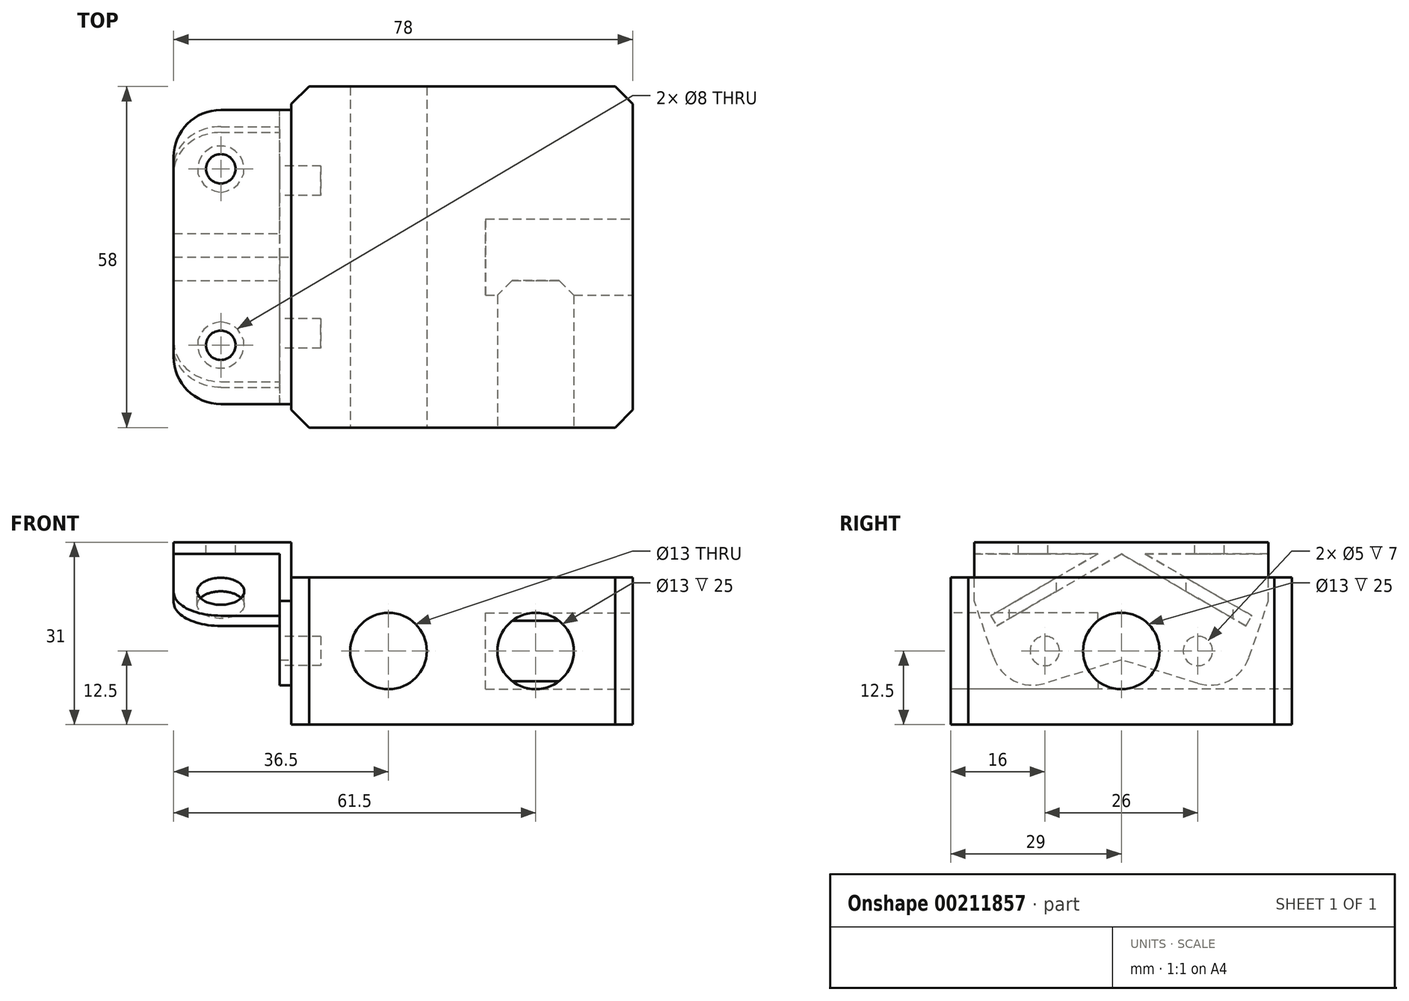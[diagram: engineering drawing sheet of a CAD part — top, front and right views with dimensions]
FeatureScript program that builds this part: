
annotation { "Feature Type Name" : "Feature", "Feature Type Description" : "" }
export const myFeature = defineFeature(function(context is Context, id is Id, definition is map)
    precondition{}
    {
        {
            var Q0;
            Q0=qCreatedBy(makeId("Top.planeOp"),FACE);
            var sketch = newSketch(context, id + "F0", { "sketchPlane" : qUnion([Q0])});
            skLineSegment(sketch, "E0.bottom", {"start": v(-29, 29) * mm, "end": v(29, 29) * mm});
            skLineSegment(sketch, "E0.top", {"start": v(-29, -29) * mm, "end": v(29, -29) * mm});
            skLineSegment(sketch, "E0.left", {"start": v(-29, 29) * mm, "end": v(-29, -29) * mm});
            skLineSegment(sketch, "E0.right", {"start": v(29, 29) * mm, "end": v(29, -29) * mm});
            skLineSegment(sketch, "E1", {"start": v(0, 0) * mm, "end": v(29, 0) * mm, "construction": true});
            skLineSegment(sketch, "E2", {"start": v(0, 0) * mm, "end": v(0, -29) * mm, "construction": true});
            skLineSegment(sketch, "E3", {"start": v(0, 0) * mm, "end": v(0, 29) * mm, "construction": true});
            skLineSegment(sketch, "E4", {"start": v(0, 0) * mm, "end": v(-29, 0) * mm, "construction": true});
            skSolve(sketch);
        }
        {
            var Q0;
            Q0 = qSketchRegion(id + "F0", true);
            extrude(context, id + "F1", {"entities" : qUnion([Q0]), "depth" : 25 * mm});
        }
        {
            var Q0;
            Q0=makeQuery(id+"F1.opExtrude","SWEPT_EDGE",EDGE,{"disambiguationData":[OSD([sQuery(id+"F0.wireOp",EDGE,"E0.top"),sQuery(id+"F0.wireOp",EDGE,"E0.left")])]});
            var Q1;
            Q1=makeQuery(id+"F1.opExtrude","SWEPT_EDGE",EDGE,{"disambiguationData":[OSD([sQuery(id+"F0.wireOp",EDGE,"E0.top"),sQuery(id+"F0.wireOp",EDGE,"E0.right")])]});
            var Q2;
            Q2=makeQuery(id+"F1.opExtrude","SWEPT_EDGE",EDGE,{"disambiguationData":[OSD([sQuery(id+"F0.wireOp",EDGE,"E0.bottom"),sQuery(id+"F0.wireOp",EDGE,"E0.right")])]});
            var Q3;
            Q3=makeQuery(id+"F1.opExtrude","SWEPT_EDGE",EDGE,{"disambiguationData":[OSD([sQuery(id+"F0.wireOp",EDGE,"E0.bottom"),sQuery(id+"F0.wireOp",EDGE,"E0.left")])]});
            chamfer(context, id + "F2", {"entities" : qUnion([Q0, Q1, Q2, Q3]), "width" : 3 * mm, "tangentPropagation" : true});
        }
        {
            var Q0;
            Q0=makeQuery(id+"F1.opExtrude","SWEPT_FACE",FACE,{"disambiguationData":[OSD([sQuery(id+"F0.wireOp",EDGE,"E0.top")])]});
            var sketch = newSketch(context, id + "F3", { "sketchPlane" : qUnion([Q0])});
            skCircle(sketch, "E5", {"center": v(-12.5, 12.5) * mm, "radius": 6.5 * mm});
            skCircle(sketch, "E6", {"center": v(12.5, 12.5) * mm, "radius": 6.5 * mm});
            skLineSegment(sketch, "E7", {"start": v(12.5, 12.5) * mm, "end": v(0, 12.5) * mm, "construction": true});
            skLineSegment(sketch, "E8", {"start": v(0, 12.5) * mm, "end": v(-12.5, 12.5) * mm, "construction": true});
            skLineSegment(sketch, "E9", {"start": v(0, 12.5) * mm, "end": v(0, 0) * mm, "construction": true});
            skLineSegment(sketch, "E10", {"start": v(0, 12.5) * mm, "end": v(0, 25) * mm, "construction": true});
            skSolve(sketch);
        }
        {
            var Q0;
            Q0=makeQuery(id+"F3.imprint","IMPRINT",FACE,{"disambiguationData":[TD([[makeQuery(id+"F3.imprint","IMPRINT",EDGE,{"derivedFrom":sQuery(id+"F3.wireOp",EDGE,"E5")}),1.0]])]});
            extrude(context, id + "F4", {"entities" : qUnion([Q0]), "operationType" : NewBodyOperationType.REMOVE, "endBound" : BoundingType.THROUGH_ALL, "oppositeDirection" : true, "depth" : 25 * mm});
        }
        {
            var Q0;
            Q0=makeQuery(id+"F3.imprint","IMPRINT",FACE,{"disambiguationData":[TD([[makeQuery(id+"F3.imprint","IMPRINT",EDGE,{"derivedFrom":sQuery(id+"F3.wireOp",EDGE,"E6")}),1.0]])]});
            extrude(context, id + "F5", {"entities" : qUnion([Q0]), "operationType" : NewBodyOperationType.REMOVE, "oppositeDirection" : true, "depth" : 25 * mm});
        }
        {
            var Q0;
            Q0=makeQuery(id+"F1.opExtrude","SWEPT_FACE",FACE,{"disambiguationData":[OSD([sQuery(id+"F0.wireOp",EDGE,"E0.right")])]});
            var sketch = newSketch(context, id + "F6", { "sketchPlane" : qUnion([Q0])});
            skCircle(sketch, "E11", {"center": v(0, 12.5) * mm, "radius": 6.5 * mm});
            skLineSegment(sketch, "E12", {"start": v(0, 25) * mm, "end": v(0, 12.5) * mm, "construction": true});
            skLineSegment(sketch, "E13", {"start": v(0, 12.5) * mm, "end": v(0, 0) * mm, "construction": true});
            skSolve(sketch);
        }
        {
            var Q0;
            Q0=makeQuery(id+"F6.imprint","IMPRINT",FACE,{"disambiguationData":[TD([[makeQuery(id+"F6.imprint","IMPRINT",EDGE,{"derivedFrom":sQuery(id+"F6.wireOp",EDGE,"E11")}),1.0]])]});
            extrude(context, id + "F7", {"entities" : qUnion([Q0]), "operationType" : NewBodyOperationType.REMOVE, "oppositeDirection" : true, "depth" : 25 * mm});
        }
        {
            var Q0;
            Q0=makeQuery(id+"F1.opExtrude","SWEPT_FACE",FACE,{"disambiguationData":[OSD([sQuery(id+"F0.wireOp",EDGE,"E0.left")])]});
            var sketch = newSketch(context, id + "F8", { "sketchPlane" : qUnion([Q0])});
            skCircle(sketch, "E14", {"center": v(-13, 12.5) * mm, "radius": 2.5 * mm});
            skCircle(sketch, "E15", {"center": v(13, 12.5) * mm, "radius": 2.5 * mm});
            skLineSegment(sketch, "E16", {"start": v(13, 12.5) * mm, "end": v(0, 12.5) * mm, "construction": true});
            skLineSegment(sketch, "E17", {"start": v(0, 12.5) * mm, "end": v(-13, 12.5) * mm, "construction": true});
            skLineSegment(sketch, "E18", {"start": v(0, 12.5) * mm, "end": v(0, 25) * mm, "construction": true});
            skLineSegment(sketch, "E19", {"start": v(0, 12.5) * mm, "end": v(0, 0) * mm, "construction": true});
            skSolve(sketch);
        }
        {
            var Q0;
            Q0=makeQuery(id+"F8.imprint","IMPRINT",FACE,{"disambiguationData":[TD([[makeQuery(id+"F8.imprint","IMPRINT",EDGE,{"derivedFrom":sQuery(id+"F8.wireOp",EDGE,"E14")}),1.0]])]});
            var Q1;
            Q1=makeQuery(id+"F8.imprint","IMPRINT",FACE,{"disambiguationData":[TD([[makeQuery(id+"F8.imprint","IMPRINT",EDGE,{"derivedFrom":sQuery(id+"F8.wireOp",EDGE,"E15")}),1.0]])]});
            extrude(context, id + "F9", {"entities" : qUnion([Q0, Q1]), "operationType" : NewBodyOperationType.REMOVE, "oppositeDirection" : true, "depth" : 5 * mm});
        }
        {
            var Q0;
            Q0=makeQuery(id+"F1.opExtrude","SWEPT_FACE",FACE,{"disambiguationData":[OSD([sQuery(id+"F0.wireOp",EDGE,"E0.left")])]});
            var sketch = newSketch(context, id + "F10", { "sketchPlane" : qUnion([Q0])});
            skLineSegment(sketch, "E20", {"start": v(-21.7, 11.41) * mm, "end": v(-25, 21) * mm});
            skLineSegment(sketch, "E21", {"start": v(-13.03, 7) * mm, "end": v(0, 11) * mm});
            skLineSegment(sketch, "E22", {"start": v(0, 11) * mm, "end": v(13.03, 7) * mm});
            skLineSegment(sketch, "E23", {"start": v(21.7, 11.41) * mm, "end": v(25, 21) * mm});
            skLineSegment(sketch, "E24", {"start": v(25, 21) * mm, "end": v(25, 31) * mm});
            skLineSegment(sketch, "E25", {"start": v(-25, 21) * mm, "end": v(-25, 31) * mm});
            skLineSegment(sketch, "E26", {"start": v(-25, 31) * mm, "end": v(0, 31) * mm});
            skLineSegment(sketch, "E27", {"start": v(0, 31) * mm, "end": v(25, 31) * mm});
            skPoint(sketch, "E28.visualSharp", {"position": v(-19.5, 5.01) * mm});
            skArc(sketch, "E28.filletArc", {"start": v(-21.7, 11.41) * mm, "mid": v(-18.25, 7.45) * mm, "end": v(-13.03, 7) * mm});
            skPoint(sketch, "E29.visualSharp", {"position": v(19.5, 5.01) * mm});
            skArc(sketch, "E29.filletArc", {"start": v(13.03, 7) * mm, "mid": v(18.25, 7.45) * mm, "end": v(21.7, 11.41) * mm});
            skLineSegment(sketch, "E30", {"start": v(15.08, 13.7) * mm, "end": v(0, 13.7) * mm, "construction": true});
            skLineSegment(sketch, "E31", {"start": v(0, 13.7) * mm, "end": v(-15.08, 13.7) * mm, "construction": true});
            skCircle(sketch, "E32", {"center": v(-13, 12.5) * mm, "radius": 3.5 * mm, "construction": true});
            skCircle(sketch, "E33", {"center": v(13, 12.5) * mm, "radius": 3.5 * mm, "construction": true});
            skLineSegment(sketch, "E34", {"start": v(-25, 29) * mm, "end": v(25, 29) * mm});
            skLineSegment(sketch, "E35", {"start": v(-22.19, 18.5) * mm, "end": v(-21.19, 16.77) * mm});
            skLineSegment(sketch, "E36", {"start": v(-21.19, 16.77) * mm, "end": v(0, 29) * mm});
            skLineSegment(sketch, "E37", {"start": v(-22.19, 18.5) * mm, "end": v(-4, 29) * mm});
            skLineSegment(sketch, "E38", {"start": v(0, 29) * mm, "end": v(21.19, 16.77) * mm});
            skLineSegment(sketch, "E39", {"start": v(21.19, 16.77) * mm, "end": v(22.19, 18.5) * mm});
            skLineSegment(sketch, "E40", {"start": v(22.19, 18.5) * mm, "end": v(4, 29) * mm});
            skSolve(sketch);
        }
        {
            var Q0;
            {var subQ5=sQuery(id+"F10.wireOp",EDGE,"E20");Q0=makeQuery(id+"F10.imprint","IMPRINT",FACE,{"disambiguationData":[TD([[makeQuery(id+"F10.imprint","IMPRINT",EDGE,{"derivedFrom":subQ5}),-1.0]])]});}
            var Q1;
            {var subQ0=sQuery(id+"F10.wireOp",EDGE,"E34");var subQ1=sQuery(id+"F10.wireOp",EDGE,"E25");var subQ2=makeQuery(id+"F10.imprint","INTERSECT",VERTEX,{"derivedFrom":[subQ1,subQ0]});Q1=makeQuery(id+"F10.imprint","IMPRINT",FACE,{"disambiguationData":[TD([[makeQuery(id+"F10.imprint","IMPRINT",EDGE,{"disambiguationData":[TD([[subQ2,1.0]])],"derivedFrom":subQ1}),-1.0]])]});}
            var Q2;
            {var subQ1=sQuery(id+"F10.wireOp",EDGE,"E34");var subQ3=sQuery(id+"F10.wireOp",EDGE,"E37");var subQ4=makeQuery(id+"F10.imprint","INTERSECT",VERTEX,{"derivedFrom":[subQ1,subQ3]});Q2=makeQuery(id+"F10.imprint","IMPRINT",FACE,{"disambiguationData":[TD([[makeQuery(id+"F10.imprint","IMPRINT",EDGE,{"disambiguationData":[TD([[subQ4,1.0]])],"derivedFrom":subQ3}),-1.0]])]});}
            var Q3;
            {var subQ1=sQuery(id+"F10.wireOp",EDGE,"E36");var subQ3=makeQuery(id+"F1.opExtrude","CAP_EDGE",EDGE,{"disambiguationData":[OSD([sQuery(id+"F0.wireOp",EDGE,"E0.left")])],"isStart":false});var subQ4=makeQuery(id+"F10.imprint","INTERSECT",VERTEX,{"derivedFrom":[subQ3,subQ1]});Q3=makeQuery(id+"F10.imprint","IMPRINT",FACE,{"disambiguationData":[TD([[makeQuery(id+"F10.imprint","IMPRINT",EDGE,{"disambiguationData":[TD([[subQ4,-1.0]])],"derivedFrom":subQ3}),1.0]])]});}
            var Q4;
            {var subQ0=sQuery(id+"F10.wireOp",EDGE,"E35");Q4=makeQuery(id+"F10.imprint","IMPRINT",FACE,{"disambiguationData":[TD([[makeQuery(id+"F10.imprint","IMPRINT",EDGE,{"derivedFrom":subQ0}),1.0]])]});}
            var Q5;
            {var subQ0=sQuery(id+"F10.wireOp",EDGE,"E39");Q5=makeQuery(id+"F10.imprint","IMPRINT",FACE,{"disambiguationData":[TD([[makeQuery(id+"F10.imprint","IMPRINT",EDGE,{"derivedFrom":subQ0}),1.0]])]});}
            var Q6;
            {var subQ1=sQuery(id+"F10.wireOp",EDGE,"E34");var subQ3=sQuery(id+"F10.wireOp",EDGE,"E40");var subQ4=makeQuery(id+"F10.imprint","INTERSECT",VERTEX,{"derivedFrom":[subQ1,subQ3]});Q6=makeQuery(id+"F10.imprint","IMPRINT",FACE,{"disambiguationData":[TD([[makeQuery(id+"F10.imprint","IMPRINT",EDGE,{"disambiguationData":[TD([[subQ4,1.0]])],"derivedFrom":subQ3}),1.0]])]});}
            var Q7;
            {var subQ0=sQuery(id+"F10.wireOp",EDGE,"E34");var subQ1=sQuery(id+"F10.wireOp",EDGE,"E24");var subQ2=makeQuery(id+"F10.imprint","INTERSECT",VERTEX,{"derivedFrom":[subQ1,subQ0]});Q7=makeQuery(id+"F10.imprint","IMPRINT",FACE,{"disambiguationData":[TD([[makeQuery(id+"F10.imprint","IMPRINT",EDGE,{"disambiguationData":[TD([[subQ2,1.0]])],"derivedFrom":subQ1}),1.0]])]});}
            var Q8;
            {var subQ0=sQuery(id+"F10.wireOp",EDGE,"E26");Q8=makeQuery(id+"F10.imprint","IMPRINT",FACE,{"disambiguationData":[TD([[makeQuery(id+"F10.imprint","IMPRINT",EDGE,{"derivedFrom":subQ0}),-1.0]])]});}
            extrude(context, id + "F11", {"entities" : qUnion([Q0, Q1, Q2, Q3, Q4, Q5, Q6, Q7, Q8]), "depth" : 2 * mm});
        }
        {
            var Q0;
            {var subQ0=sQuery(id+"F10.wireOp",EDGE,"E26");Q0=makeQuery(id+"F10.imprint","IMPRINT",FACE,{"disambiguationData":[TD([[makeQuery(id+"F10.imprint","IMPRINT",EDGE,{"derivedFrom":subQ0}),-1.0]])]});}
            var Q1;
            {var subQ1=sQuery(id+"F10.wireOp",EDGE,"E34");var subQ3=sQuery(id+"F10.wireOp",EDGE,"E37");var subQ4=makeQuery(id+"F10.imprint","INTERSECT",VERTEX,{"derivedFrom":[subQ1,subQ3]});Q1=makeQuery(id+"F10.imprint","IMPRINT",FACE,{"disambiguationData":[TD([[makeQuery(id+"F10.imprint","IMPRINT",EDGE,{"disambiguationData":[TD([[subQ4,1.0]])],"derivedFrom":subQ3}),-1.0]])]});}
            var Q2;
            {var subQ0=sQuery(id+"F10.wireOp",EDGE,"E35");Q2=makeQuery(id+"F10.imprint","IMPRINT",FACE,{"disambiguationData":[TD([[makeQuery(id+"F10.imprint","IMPRINT",EDGE,{"derivedFrom":subQ0}),1.0]])]});}
            var Q3;
            {var subQ1=sQuery(id+"F10.wireOp",EDGE,"E34");var subQ3=sQuery(id+"F10.wireOp",EDGE,"E40");var subQ4=makeQuery(id+"F10.imprint","INTERSECT",VERTEX,{"derivedFrom":[subQ1,subQ3]});Q3=makeQuery(id+"F10.imprint","IMPRINT",FACE,{"disambiguationData":[TD([[makeQuery(id+"F10.imprint","IMPRINT",EDGE,{"disambiguationData":[TD([[subQ4,1.0]])],"derivedFrom":subQ3}),1.0]])]});}
            var Q4;
            {var subQ0=sQuery(id+"F10.wireOp",EDGE,"E39");Q4=makeQuery(id+"F10.imprint","IMPRINT",FACE,{"disambiguationData":[TD([[makeQuery(id+"F10.imprint","IMPRINT",EDGE,{"derivedFrom":subQ0}),1.0]])]});}
            extrude(context, id + "F12", {"entities" : qUnion([Q0, Q1, Q2, Q3, Q4]), "operationType" : NewBodyOperationType.ADD, "depth" : 20 * mm});
        }
        {
            var Q0;
            {var subQ0=sQuery(id+"F10.wireOp",EDGE,"E27");var subQ1=sQuery(id+"F10.wireOp",EDGE,"E26");Q0=makeQuery(id+"F12.boolean.opBoolean","MERGE",FACE,{"derivedFrom":[makeQuery(id+"F11.opExtrude","SWEPT_FACE",FACE,{"disambiguationData":[OSD([subQ1,subQ0])]}),makeQuery(id+"F12.opExtrude","SWEPT_FACE",FACE,{"disambiguationData":[OSD([subQ1,subQ0])]})]});}
            var sketch = newSketch(context, id + "F13", { "sketchPlane" : qUnion([Q0])});
            skCircle(sketch, "E41", {"center": v(-41, 15) * mm, "radius": 2.5 * mm});
            skCircle(sketch, "E42", {"center": v(-41, -15) * mm, "radius": 2.5 * mm});
            skLineSegment(sketch, "E43", {"start": v(-41, 0) * mm, "end": v(-41, -15) * mm, "construction": true});
            skLineSegment(sketch, "E44", {"start": v(-41, 0) * mm, "end": v(-41, 15) * mm, "construction": true});
            skLineSegment(sketch, "E45", {"start": v(-49, 0) * mm, "end": v(-41, 0) * mm});
            skCircle(sketch, "E46", {"center": v(-41, 15) * mm, "radius": 4 * mm});
            skCircle(sketch, "E47", {"center": v(-41, -15) * mm, "radius": 4 * mm});
            skSolve(sketch);
        }
        {
            var Q0;
            Q0=makeQuery(id+"F13.imprint","IMPRINT",FACE,{"disambiguationData":[TD([[makeQuery(id+"F13.imprint","IMPRINT",EDGE,{"derivedFrom":sQuery(id+"F13.wireOp",EDGE,"E42")}),1.0]])]});
            var Q1;
            Q1=makeQuery(id+"F13.imprint","IMPRINT",FACE,{"disambiguationData":[TD([[makeQuery(id+"F13.imprint","IMPRINT",EDGE,{"derivedFrom":sQuery(id+"F13.wireOp",EDGE,"E41")}),1.0]])]});
            extrude(context, id + "F14", {"entities" : qUnion([Q0, Q1]), "operationType" : NewBodyOperationType.REMOVE, "oppositeDirection" : true, "depth" : 3 * mm});
        }
        {
            var Q0;
            Q0=makeQuery(id+"F13.imprint","IMPRINT",FACE,{"disambiguationData":[TD([[makeQuery(id+"F13.imprint","IMPRINT",EDGE,{"derivedFrom":sQuery(id+"F13.wireOp",EDGE,"E41")}),-1.0]])]});
            var Q1;
            Q1=makeQuery(id+"F13.imprint","IMPRINT",FACE,{"disambiguationData":[TD([[makeQuery(id+"F13.imprint","IMPRINT",EDGE,{"derivedFrom":sQuery(id+"F13.wireOp",EDGE,"E42")}),-1.0]])]});
            var Q2;
            Q2=makeQuery(id+"F13.imprint","IMPRINT",FACE,{"disambiguationData":[TD([[makeQuery(id+"F13.imprint","IMPRINT",EDGE,{"derivedFrom":sQuery(id+"F13.wireOp",EDGE,"E42")}),1.0]])]});
            var Q3;
            Q3=makeQuery(id+"F13.imprint","IMPRINT",FACE,{"disambiguationData":[TD([[makeQuery(id+"F13.imprint","IMPRINT",EDGE,{"derivedFrom":sQuery(id+"F13.wireOp",EDGE,"E41")}),1.0]])]});
            var Q4;
            Q4=sQuery(id+"F13.wireOp",EDGE,"E47");
            var Q5;
            Q5=sQuery(id+"F13.wireOp",EDGE,"E46");
            extrude(context, id + "F15", {"entities" : qUnion([Q0, Q1, Q2, Q3]), "operationType" : NewBodyOperationType.REMOVE, "surfaceEntities" : qUnion([Q4, Q5]), "endBound" : BoundingType.THROUGH_ALL, "oppositeDirection" : true, "depth" : 25 * mm, "hasSecondDirection" : true, "secondDirectionOppositeDirection" : true, "secondDirectionDepth" : 3 * mm});
        }
        {
            var Q0;
            Q0=makeQuery(id+"F12.opExtrude","CAP_EDGE",EDGE,{"disambiguationData":[OSD([sQuery(id+"F10.wireOp",EDGE,"E25")])],"isStart":false});
            var Q1;
            Q1=makeQuery(id+"F12.opExtrude","CAP_EDGE",EDGE,{"disambiguationData":[OSD([sQuery(id+"F10.wireOp",EDGE,"E35")])],"isStart":false});
            var Q2;
            Q2=makeQuery(id+"F12.opExtrude","CAP_EDGE",EDGE,{"disambiguationData":[OSD([sQuery(id+"F10.wireOp",EDGE,"E24")])],"isStart":false});
            var Q3;
            Q3=makeQuery(id+"F12.opExtrude","CAP_EDGE",EDGE,{"disambiguationData":[OSD([sQuery(id+"F10.wireOp",EDGE,"E39")])],"isStart":false});
            fillet(context, id + "F16", {"entities" : qUnion([Q0, Q1, Q2, Q3]), "radius" : 8 * mm, "tangentPropagation" : true, "allowEdgeOverflow" : false});
        }
    });
